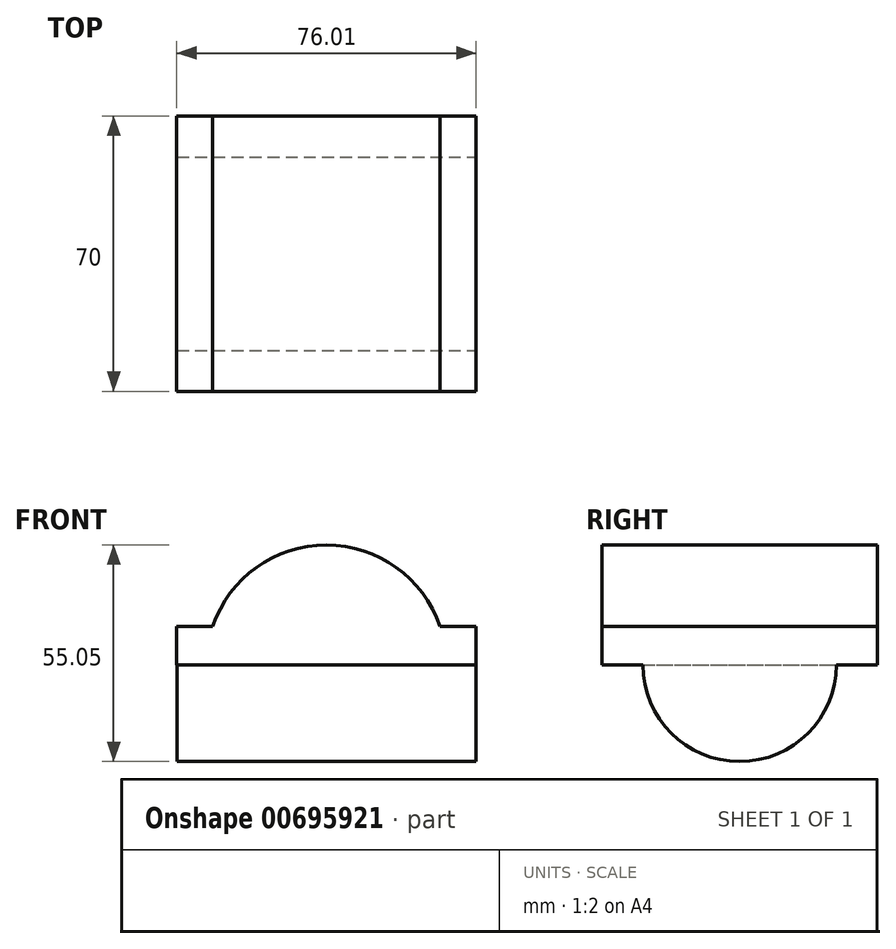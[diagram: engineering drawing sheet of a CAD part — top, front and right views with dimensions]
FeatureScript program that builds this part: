
annotation { "Feature Type Name" : "Feature", "Feature Type Description" : "" }
export const myFeature = defineFeature(function(context is Context, id is Id, definition is map)
    precondition{}
    {
        {
            var Q0;
            Q0=qCreatedBy(makeId("Front.planeOp"),FACE);
            var sketch = newSketch(context, id + "F0", { "sketchPlane" : qUnion([Q0])});
            skLineSegment(sketch, "E0", {"start": v(-51, 25.15) * mm, "end": v(-41.86, 25.15) * mm});
            skLineSegment(sketch, "E1", {"start": v(25, 25.15) * mm, "end": v(25, 15.3) * mm});
            skLineSegment(sketch, "E2", {"start": v(25, 15.3) * mm, "end": v(-51, 15.3) * mm});
            skLineSegment(sketch, "E3", {"start": v(-51, 15.3) * mm, "end": v(-51, 25.15) * mm});
            skArc(sketch, "E4", {"start": v(15.85, 25.15) * mm, "mid": v(-13, 45.8) * mm, "end": v(-41.86, 25.15) * mm});
            skLineSegment(sketch, "E5.trimOffspring", {"start": v(15.85, 25.15) * mm, "end": v(25, 25.15) * mm});
            skSolve(sketch);
        }
        {
            var Q0;
            Q0 = qSketchRegion(id + "F0", true);
            extrude(context, id + "F1", {"entities" : qUnion([Q0]), "depth" : 70 * mm, "offsetDistance" : 25 * mm});
        }
        {
            var Q0;
            Q0=makeQuery(id+"F1.opExtrude","SWEPT_FACE",FACE,{"disambiguationData":[OSD([sQuery(id+"F0.wireOp",EDGE,"E1")])]});
            var sketch = newSketch(context, id + "F2", { "sketchPlane" : qUnion([Q0])});
            skPoint(sketch, "E6.center.orphan", {"position": v(-35, 15.3) * mm});
            skArc(sketch, "E7", {"start": v(-59.56, 15.3) * mm, "mid": v(-35, -9.25) * mm, "end": v(-10.44, 15.3) * mm});
            skPoint(sketch, "E8", {"position": v(-59.56, 15.3) * mm});
            skPoint(sketch, "E9", {"position": v(-10.44, 15.3) * mm});
            skSolve(sketch);
        }
        {
            var Q0;
            Q0 = qSketchRegion(id + "F2", true);
            var Q1;
            {var subQ0=sQuery(id+"F2.wireOp",EDGE,"E7");Q1=makeQuery(id+"F2.imprint","IMPRINT",FACE,{"disambiguationData":[TD([[makeQuery(id+"F2.imprint","IMPRINT",EDGE,{"derivedFrom":subQ0}),1.0]])]});}
            extrude(context, id + "F3", {"entities" : qUnion([Q0, Q1]), "operationType" : NewBodyOperationType.ADD, "oppositeDirection" : true, "depth" : 75.9 * mm, "offsetDistance" : 25 * mm});
        }
    });
